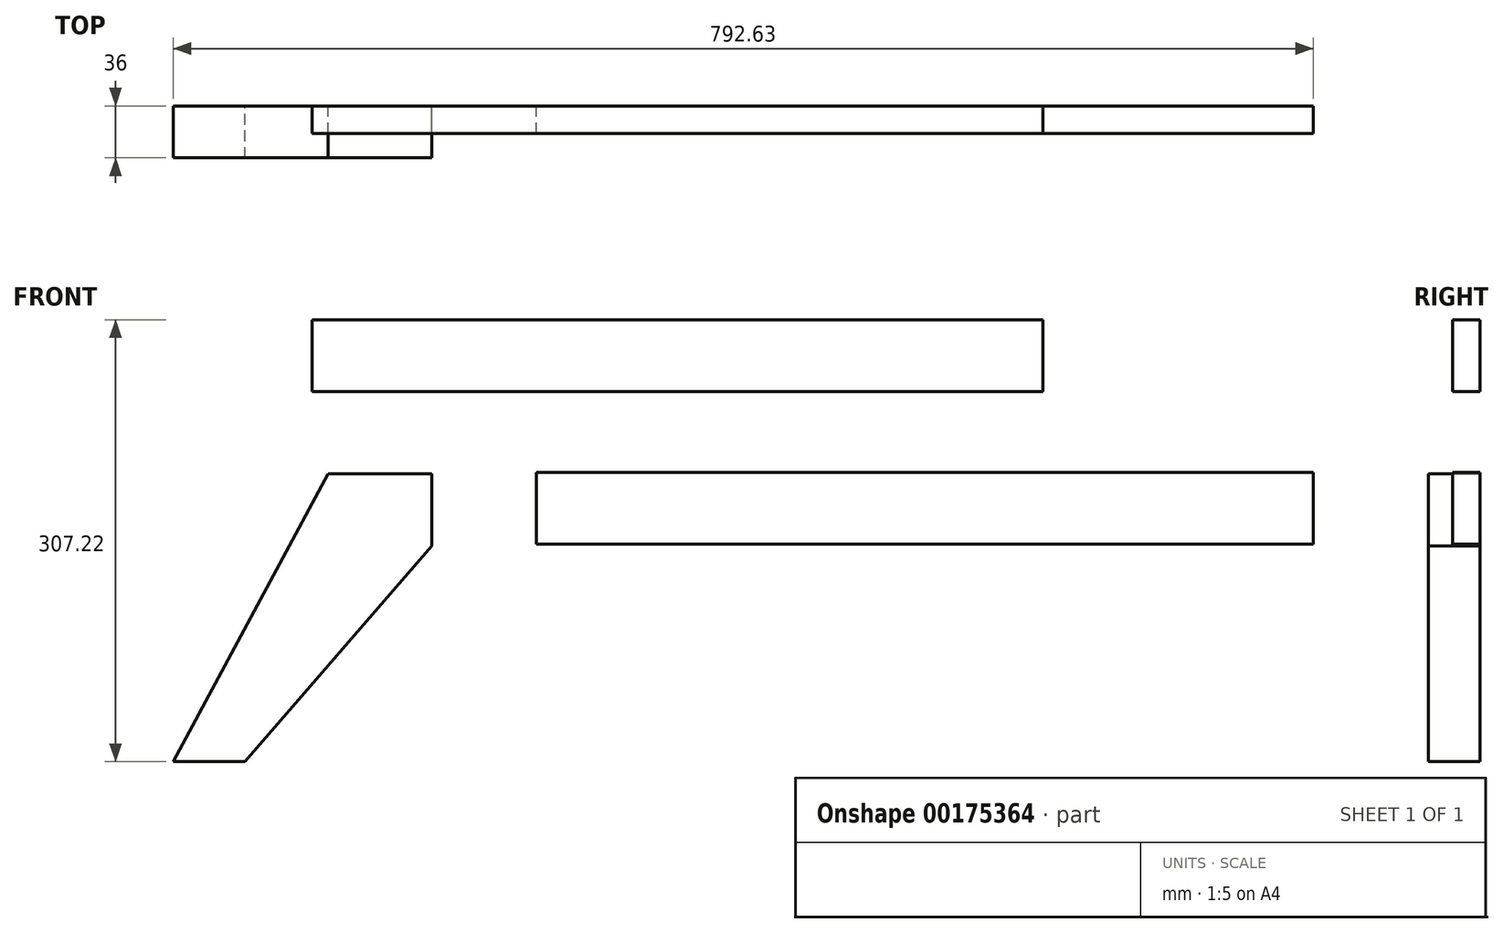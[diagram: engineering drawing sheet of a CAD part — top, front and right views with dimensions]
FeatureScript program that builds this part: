
annotation { "Feature Type Name" : "Feature", "Feature Type Description" : "" }
export const myFeature = defineFeature(function(context is Context, id is Id, definition is map)
    precondition{}
    {
        {
            var Q0;
            Q0=qCreatedBy(makeId("Front.planeOp"),FACE);
            var sketch = newSketch(context, id + "F0", { "sketchPlane" : qUnion([Q0])});
            skLineSegment(sketch, "E0", {"start": v(-13.1, 99.13) * mm, "end": v(59, 99.13) * mm});
            skLineSegment(sketch, "E1", {"start": v(59, 99.13) * mm, "end": v(59, 49.13) * mm});
            skLineSegment(sketch, "E2", {"start": v(59, 49.13) * mm, "end": v(-71, -100.87) * mm});
            skLineSegment(sketch, "E3", {"start": v(-71, -100.87) * mm, "end": v(-121, -100.87) * mm});
            skLineSegment(sketch, "E4", {"start": v(-121, -100.87) * mm, "end": v(-13.1, 99.13) * mm});
            skSolve(sketch);
        }
        {
            var Q0;
            Q0=makeQuery(id+"F0.imprint","IMPRINT",FACE,{"disambiguationData":[TD([[makeQuery(id+"F0.imprint","IMPRINT",EDGE,{"derivedFrom":sQuery(id+"F0.wireOp",EDGE,"E0")}),-1.0]])]});
            extrude(context, id + "F1", {"entities" : qUnion([Q0]), "depth" : 36 * mm});
        }
        {
            var Q0;
            Q0=qCreatedBy(makeId("Front.planeOp"),FACE);
            var sketch = newSketch(context, id + "F2", { "sketchPlane" : qUnion([Q0])});
            skLineSegment(sketch, "E5.bottom", {"start": v(131.63, 50.24) * mm, "end": v(671.63, 50.24) * mm});
            skLineSegment(sketch, "E5.top", {"start": v(131.63, 100.24) * mm, "end": v(671.63, 100.24) * mm});
            skLineSegment(sketch, "E5.left", {"start": v(131.63, 50.24) * mm, "end": v(131.63, 100.24) * mm});
            skLineSegment(sketch, "E5.right", {"start": v(671.63, 50.24) * mm, "end": v(671.63, 100.24) * mm});
            skSolve(sketch);
        }
        {
            var Q0;
            Q0=makeQuery(id+"F2.imprint","IMPRINT",FACE,{"disambiguationData":[TD([[makeQuery(id+"F2.imprint","IMPRINT",EDGE,{"derivedFrom":sQuery(id+"F2.wireOp",EDGE,"E5.bottom")}),1.0]])]});
            extrude(context, id + "F3", {"entities" : qUnion([Q0]), "depth" : 19 * mm});
        }
        {
            var Q0;
            Q0=qCreatedBy(makeId("Front.planeOp"),FACE);
            var sketch = newSketch(context, id + "F4", { "sketchPlane" : qUnion([Q0])});
            skLineSegment(sketch, "E6.bottom", {"start": v(-24.26, 206.35) * mm, "end": v(483.74, 206.35) * mm});
            skLineSegment(sketch, "E6.top", {"start": v(-24.26, 156.35) * mm, "end": v(483.74, 156.35) * mm});
            skLineSegment(sketch, "E6.left", {"start": v(-24.26, 206.35) * mm, "end": v(-24.26, 156.35) * mm});
            skLineSegment(sketch, "E6.right", {"start": v(483.74, 206.35) * mm, "end": v(483.74, 156.35) * mm});
            skSolve(sketch);
        }
        {
            var Q0;
            Q0=makeQuery(id+"F4.imprint","IMPRINT",FACE,{"disambiguationData":[TD([[makeQuery(id+"F4.imprint","IMPRINT",EDGE,{"derivedFrom":sQuery(id+"F4.wireOp",EDGE,"E6.bottom")}),-1.0]])]});
            extrude(context, id + "F5", {"entities" : qUnion([Q0]), "depth" : 19 * mm});
        }
    });
